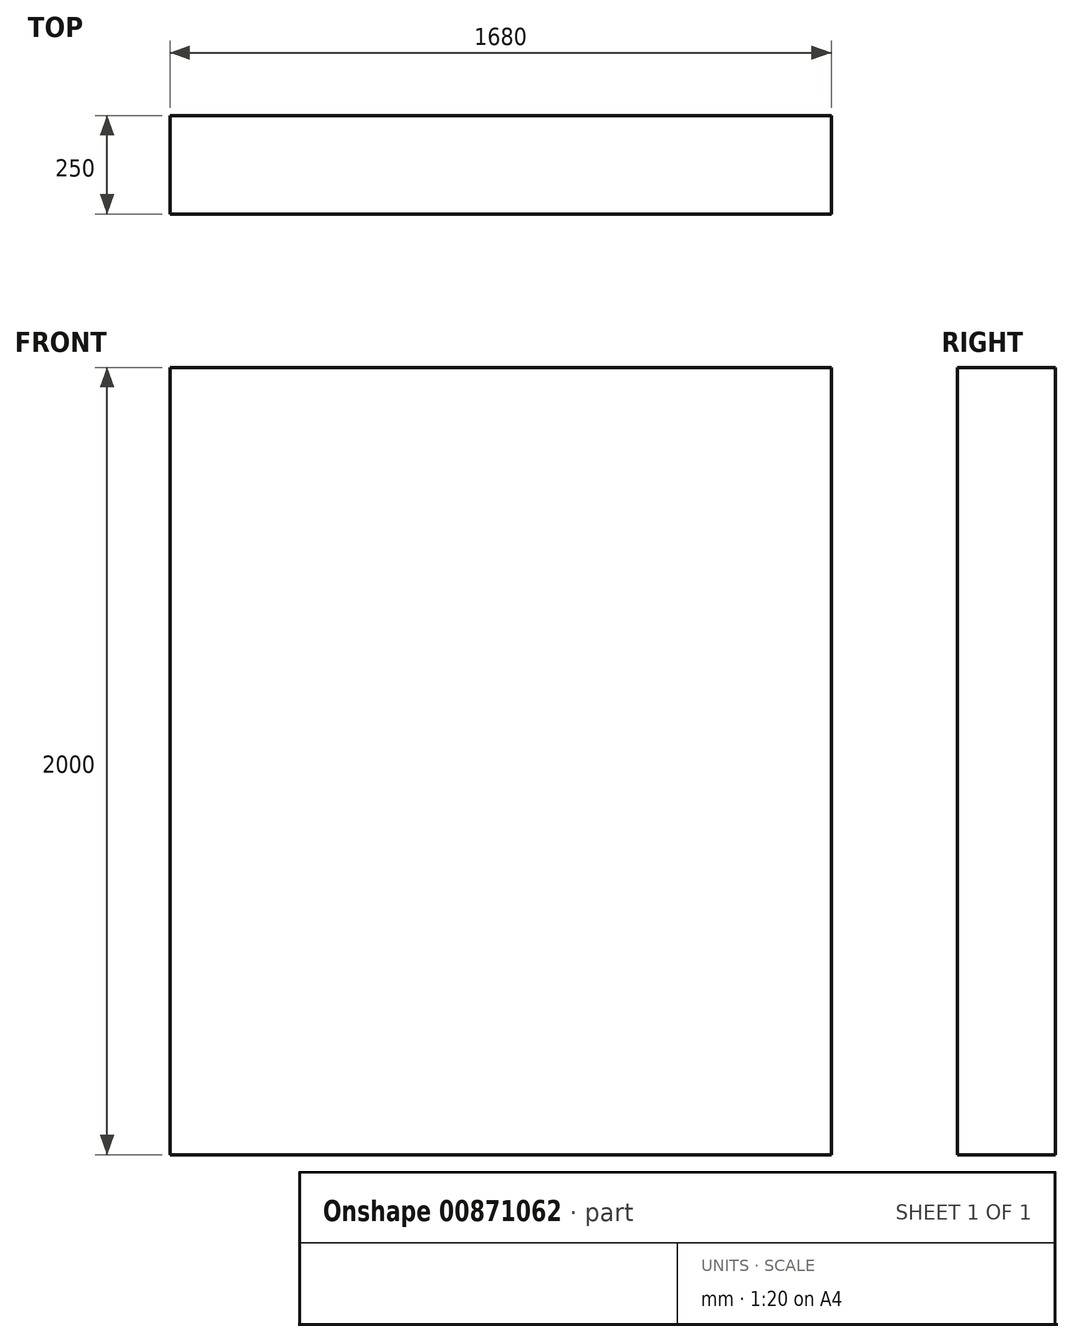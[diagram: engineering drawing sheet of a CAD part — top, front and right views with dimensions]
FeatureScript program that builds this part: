
annotation { "Feature Type Name" : "Feature", "Feature Type Description" : "" }
export const myFeature = defineFeature(function(context is Context, id is Id, definition is map)
    precondition{}
    {
        {
            var Q0;
            Q0=qCreatedBy(makeId("Front.planeOp"),FACE);
            var sketch = newSketch(context, id + "F0", { "sketchPlane" : qUnion([Q0])});
            skLineSegment(sketch, "E0.bottom", {"start": v(840, 1000) * mm, "end": v(-840, 1000) * mm});
            skLineSegment(sketch, "E0.top", {"start": v(840, -1000) * mm, "end": v(-840, -1000) * mm});
            skLineSegment(sketch, "E0.left", {"start": v(840, 1000) * mm, "end": v(840, -1000) * mm});
            skLineSegment(sketch, "E0.right", {"start": v(-840, 1000) * mm, "end": v(-840, -1000) * mm});
            skPoint(sketch, "E0.middle", {"position": v(0, 0) * mm});
            skSolve(sketch);
        }
        {
            var Q0;
            Q0=makeQuery(id+"F0.imprint","IMPRINT",FACE,{"disambiguationData":[TD([[makeQuery(id+"F0.imprint","IMPRINT",EDGE,{"derivedFrom":sQuery(id+"F0.wireOp",EDGE,"E0.bottom")}),1.0]])]});
            extrude(context, id + "F1", {"entities" : qUnion([Q0]), "oppositeDirection" : true, "depth" : 250 * mm, "offsetDistance" : 25 * mm});
        }
    });
